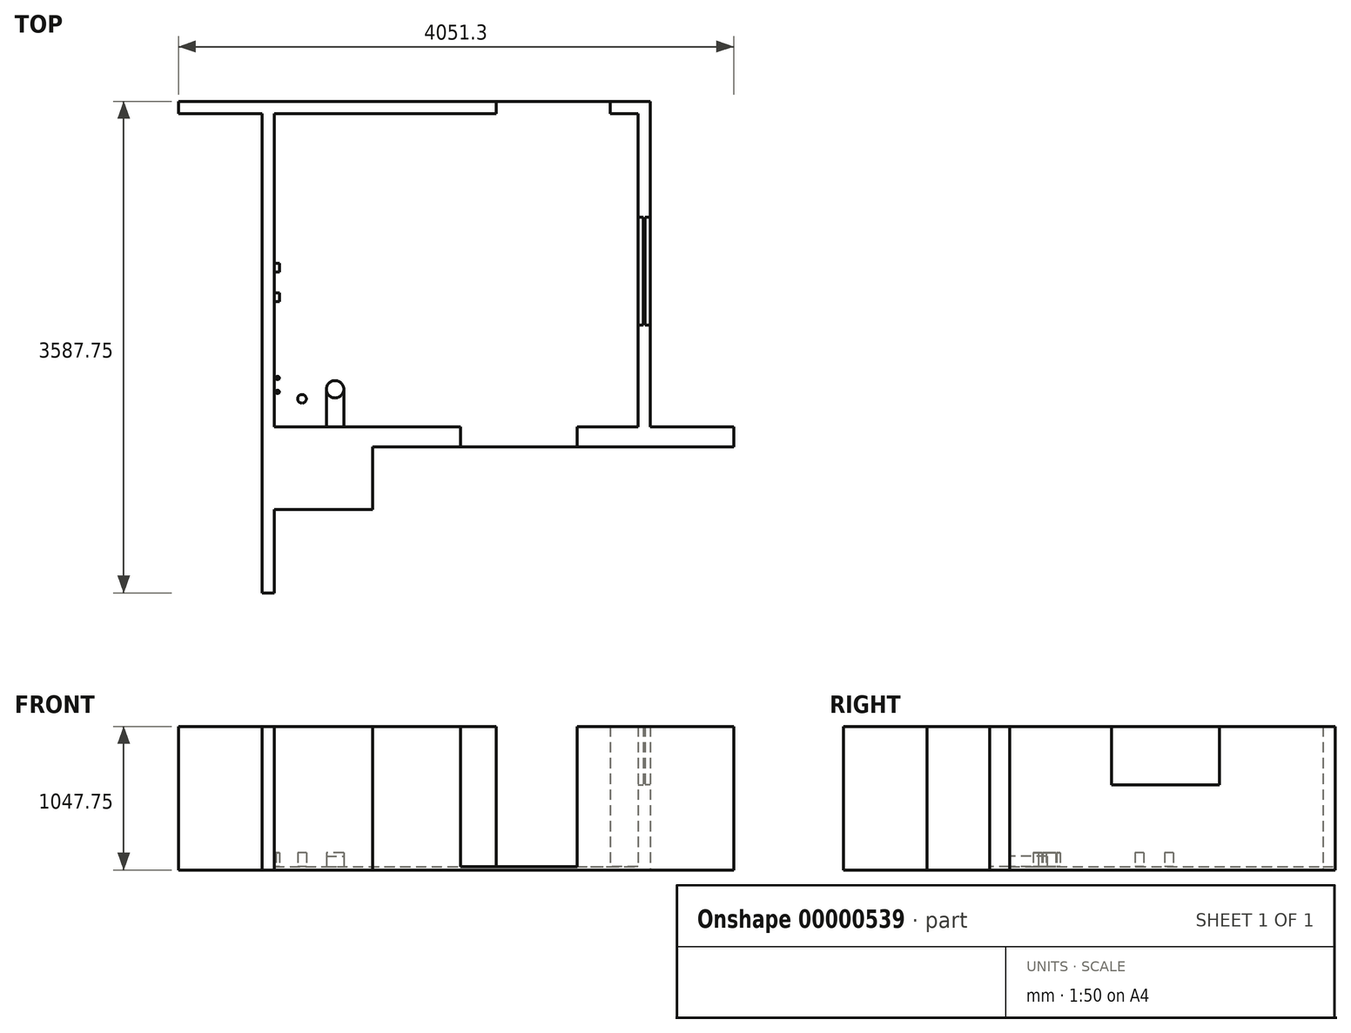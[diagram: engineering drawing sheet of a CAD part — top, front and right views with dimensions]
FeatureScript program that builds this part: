
annotation { "Feature Type Name" : "Feature", "Feature Type Description" : "" }
export const myFeature = defineFeature(function(context is Context, id is Id, definition is map)
    precondition{}
    {
        {
            var Q0;
            Q0=qCreatedBy(makeId("Top.planeOp"),FACE);
            var sketch = newSketch(context, id + "F0", { "sketchPlane" : qUnion([Q0])});
            skLineSegment(sketch, "E0.bottom", {"start": v(0, 2286) * mm, "end": v(1619.25, 2286) * mm});
            skLineSegment(sketch, "E0.top", {"start": v(0, 0) * mm, "end": v(1358.9, 0) * mm});
            skLineSegment(sketch, "E0.left", {"start": v(0, 2286) * mm, "end": v(0, 0) * mm});
            skLineSegment(sketch, "E1", {"start": v(1358.9, 0) * mm, "end": v(1358.9, -146.05) * mm});
            skLineSegment(sketch, "E2", {"start": v(1358.9, -146.05) * mm, "end": v(717.55, -146.05) * mm});
            skLineSegment(sketch, "E3", {"start": v(717.55, -146.05) * mm, "end": v(717.55, -603.25) * mm});
            skLineSegment(sketch, "E4", {"start": v(717.55, -603.25) * mm, "end": v(0, -603.25) * mm});
            skLineSegment(sketch, "E5", {"start": v(0, -603.25) * mm, "end": v(0, -1212.85) * mm});
            skLineSegment(sketch, "E6", {"start": v(2209.8, -146.05) * mm, "end": v(2209.8, 0) * mm});
            skLineSegment(sketch, "E7", {"start": v(2209.8, 0) * mm, "end": v(2654.3, 0) * mm});
            skLineSegment(sketch, "E8", {"start": v(2654.3, 0) * mm, "end": v(2654.3, 2286) * mm});
            skLineSegment(sketch, "E9", {"start": v(2654.3, 2286) * mm, "end": v(2451.1, 2286) * mm});
            skLineSegment(sketch, "E10", {"start": v(2451.1, 2286) * mm, "end": v(2451.1, 2374.9) * mm});
            skLineSegment(sketch, "E11", {"start": v(2451.1, 2374.9) * mm, "end": v(2743.2, 2374.9) * mm});
            skLineSegment(sketch, "E12", {"start": v(2743.2, 2374.9) * mm, "end": v(2743.2, 0) * mm});
            skLineSegment(sketch, "E13", {"start": v(2743.2, 0) * mm, "end": v(3352.8, 0) * mm});
            skLineSegment(sketch, "E14", {"start": v(1619.25, 2286) * mm, "end": v(1619.25, 2374.9) * mm});
            skLineSegment(sketch, "E15", {"start": v(1619.25, 2374.9) * mm, "end": v(-698.5, 2374.9) * mm});
            skLineSegment(sketch, "E16", {"start": v(-698.5, 2374.9) * mm, "end": v(-698.5, 2286) * mm});
            skLineSegment(sketch, "E17", {"start": v(-698.5, 2286) * mm, "end": v(-88.9, 2286) * mm});
            skLineSegment(sketch, "E18", {"start": v(-88.9, 2286) * mm, "end": v(-88.9, -1212.85) * mm});
            skLineSegment(sketch, "E19", {"start": v(2209.8, -146.05) * mm, "end": v(3352.8, -146.05) * mm});
            skLineSegment(sketch, "E20", {"start": v(3352.8, -146.05) * mm, "end": v(3352.8, 0) * mm});
            skLineSegment(sketch, "E21", {"start": v(-88.9, -1212.85) * mm, "end": v(0, -1212.85) * mm});
            skSolve(sketch);
        }
        {
            var Q0;
            Q0 = qSketchRegion(id + "F0", true);
            extrude(context, id + "F1", {"entities" : qUnion([Q0]), "depth" : 2241.55 * mm, "offsetDistance" : 25.4 * mm});
        }
        {
            var Q0;
            Q0=qCreatedBy(makeId("Top.planeOp"),FACE);
            var sketch = newSketch(context, id + "F2", { "sketchPlane" : qUnion([Q0])});
            skLineSegment(sketch, "E22.0", {"start": v(2743.2, 0) * mm, "end": v(3352.8, 0) * mm});
            skLineSegment(sketch, "E22.1", {"start": v(2743.2, 2374.9) * mm, "end": v(2743.2, 0) * mm});
            skLineSegment(sketch, "E22.2", {"start": v(2451.1, 2374.9) * mm, "end": v(2743.2, 2374.9) * mm});
            skLineSegment(sketch, "E22.3", {"start": v(-698.5, 2374.9) * mm, "end": v(-698.5, 2286) * mm});
            skLineSegment(sketch, "E22.4", {"start": v(-698.5, 2286) * mm, "end": v(-88.9, 2286) * mm});
            skLineSegment(sketch, "E22.5", {"start": v(-88.9, 2286) * mm, "end": v(-88.9, -1212.85) * mm});
            skLineSegment(sketch, "E23", {"start": v(-698.5, 2374.9) * mm, "end": v(2451.1, 2374.9) * mm});
            skLineSegment(sketch, "E24", {"start": v(3352.8, 0) * mm, "end": v(3352.8, -146.05) * mm});
            skLineSegment(sketch, "E25", {"start": v(3352.8, -146.05) * mm, "end": v(717.55, -146.05) * mm});
            skLineSegment(sketch, "E26", {"start": v(717.55, -146.05) * mm, "end": v(717.55, -603.25) * mm});
            skLineSegment(sketch, "E27", {"start": v(717.55, -603.25) * mm, "end": v(0, -603.25) * mm});
            skLineSegment(sketch, "E28", {"start": v(0, -603.25) * mm, "end": v(0, -1212.85) * mm});
            skLineSegment(sketch, "E29", {"start": v(0, -1212.85) * mm, "end": v(-88.9, -1212.85) * mm});
            skSolve(sketch);
        }
        {
            var Q0;
            Q0 = qSketchRegion(id + "F2", true);
            extrude(context, id + "F3", {"entities" : qUnion([Q0]), "oppositeDirection" : true, "depth" : 25.4 * mm, "offsetDistance" : 25.4 * mm});
        }
        {
            var Q0;
            Q0=makeQuery(id+"F1.opExtrude","SWEPT_BODY",BODY,{"disambiguationData":[OSD([sQuery(id+"F0.wireOp",EDGE,"E0.bottom"),sQuery(id+"F0.wireOp",EDGE,"E0.top"),sQuery(id+"F0.wireOp",EDGE,"E0.left"),sQuery(id+"F0.wireOp",EDGE,"E1"),sQuery(id+"F0.wireOp",EDGE,"E2"),sQuery(id+"F0.wireOp",EDGE,"E3"),sQuery(id+"F0.wireOp",EDGE,"E4"),sQuery(id+"F0.wireOp",EDGE,"E5"),sQuery(id+"F0.wireOp",EDGE,"E14"),sQuery(id+"F0.wireOp",EDGE,"E15"),sQuery(id+"F0.wireOp",EDGE,"E16"),sQuery(id+"F0.wireOp",EDGE,"E17"),sQuery(id+"F0.wireOp",EDGE,"E18"),sQuery(id+"F0.wireOp",EDGE,"E21")])]});
            var Q1;
            Q1=makeQuery(id+"F1.opExtrude","SWEPT_BODY",BODY,{"disambiguationData":[OSD([sQuery(id+"F0.wireOp",EDGE,"E6"),sQuery(id+"F0.wireOp",EDGE,"E7"),sQuery(id+"F0.wireOp",EDGE,"E8"),sQuery(id+"F0.wireOp",EDGE,"E9"),sQuery(id+"F0.wireOp",EDGE,"E10"),sQuery(id+"F0.wireOp",EDGE,"E11"),sQuery(id+"F0.wireOp",EDGE,"E12"),sQuery(id+"F0.wireOp",EDGE,"E13"),sQuery(id+"F0.wireOp",EDGE,"E19"),sQuery(id+"F0.wireOp",EDGE,"E20")])]});
            var Q2;
            Q2=makeQuery(id+"F3.opExtrude","SWEPT_BODY",BODY,{"disambiguationData":[OSD([sQuery(id+"F2.wireOp",EDGE,"E22.0"),sQuery(id+"F2.wireOp",EDGE,"E22.1"),sQuery(id+"F2.wireOp",EDGE,"E22.2"),sQuery(id+"F2.wireOp",EDGE,"E22.3"),sQuery(id+"F2.wireOp",EDGE,"E22.4"),sQuery(id+"F2.wireOp",EDGE,"E22.5"),sQuery(id+"F2.wireOp",EDGE,"E23"),sQuery(id+"F2.wireOp",EDGE,"E24"),sQuery(id+"F2.wireOp",EDGE,"E25"),sQuery(id+"F2.wireOp",EDGE,"E26"),sQuery(id+"F2.wireOp",EDGE,"E27"),sQuery(id+"F2.wireOp",EDGE,"E28"),sQuery(id+"F2.wireOp",EDGE,"E29")])]});
            booleanBodies(context, id + "F4", {"operationType" : BooleanOperationType.UNION, "tools" : qUnion([Q0, Q1, Q2])});
        }
        {
            var Q0;
            Q0=qCreatedBy(makeId("Top.planeOp"),FACE);
            cPlane(context, id + "F5", {"entities" : qUnion([Q0]), "cplaneType" : CPlaneType.OFFSET, "offset" : 596.9 * mm, "width" : 152.4 * mm, "height" : 152.4 * mm});
        }
        {
            var Q0;
            Q0=qCreatedBy(id+"F5.planeOp",FACE);
            var sketch = newSketch(context, id + "F6", { "sketchPlane" : qUnion([Q0])});
            skLineSegment(sketch, "E30.bottom", {"start": v(2654.3, 1530.35) * mm, "end": v(2692.4, 1530.35) * mm});
            skLineSegment(sketch, "E30.top", {"start": v(2654.3, 742.95) * mm, "end": v(2692.4, 742.95) * mm});
            skLineSegment(sketch, "E30.left", {"start": v(2654.3, 1530.35) * mm, "end": v(2654.3, 742.95) * mm});
            skLineSegment(sketch, "E30.right", {"start": v(2692.4, 1530.35) * mm, "end": v(2692.4, 742.95) * mm});
            skLineSegment(sketch, "E31.bottom", {"start": v(2743.2, 742.95) * mm, "end": v(2705.1, 742.95) * mm});
            skLineSegment(sketch, "E31.top", {"start": v(2743.2, 1530.35) * mm, "end": v(2705.1, 1530.35) * mm});
            skLineSegment(sketch, "E31.left", {"start": v(2743.2, 742.95) * mm, "end": v(2743.2, 1530.35) * mm});
            skLineSegment(sketch, "E31.right", {"start": v(2705.1, 742.95) * mm, "end": v(2705.1, 1530.35) * mm});
            skSolve(sketch);
        }
        {
            var Q0;
            Q0 = qSketchRegion(id + "F6", true);
            extrude(context, id + "F7", {"entities" : qUnion([Q0]), "operationType" : NewBodyOperationType.REMOVE, "depth" : 1244.6 * mm, "offsetDistance" : 25.4 * mm});
        }
        {
            var Q0;
            Q0=makeQuery(id+"F3.opExtrude","CAP_FACE",FACE,{"disambiguationData":[OSD([sQuery(id+"F2.wireOp",EDGE,"E22.0"),sQuery(id+"F2.wireOp",EDGE,"E22.1"),sQuery(id+"F2.wireOp",EDGE,"E22.2"),sQuery(id+"F2.wireOp",EDGE,"E22.3"),sQuery(id+"F2.wireOp",EDGE,"E22.4"),sQuery(id+"F2.wireOp",EDGE,"E22.5"),sQuery(id+"F2.wireOp",EDGE,"E23"),sQuery(id+"F2.wireOp",EDGE,"E24"),sQuery(id+"F2.wireOp",EDGE,"E25"),sQuery(id+"F2.wireOp",EDGE,"E26"),sQuery(id+"F2.wireOp",EDGE,"E27"),sQuery(id+"F2.wireOp",EDGE,"E28"),sQuery(id+"F2.wireOp",EDGE,"E29")])],"isStart":true});
            var sketch = newSketch(context, id + "F8", { "sketchPlane" : qUnion([Q0])});
            skPoint(sketch, "E32.oppositeSnap0", {"position": v(0, 1130.3) * mm});
            skLineSegment(sketch, "E32.bottom", {"start": v(0, 1193.8) * mm, "end": v(38.1, 1193.8) * mm});
            skLineSegment(sketch, "E32.top", {"start": v(0, 1130.3) * mm, "end": v(38.1, 1130.3) * mm});
            skLineSegment(sketch, "E32.left", {"start": v(0, 1193.8) * mm, "end": v(0, 1130.3) * mm});
            skLineSegment(sketch, "E32.right", {"start": v(38.1, 1193.8) * mm, "end": v(38.1, 1130.3) * mm});
            skLineSegment(sketch, "E33.bottom", {"start": v(0, 914.4) * mm, "end": v(38.1, 914.4) * mm});
            skLineSegment(sketch, "E33.top", {"start": v(0, 977.9) * mm, "end": v(38.1, 977.9) * mm});
            skLineSegment(sketch, "E33.left", {"start": v(0, 914.4) * mm, "end": v(0, 977.9) * mm});
            skLineSegment(sketch, "E33.right", {"start": v(38.1, 914.4) * mm, "end": v(38.1, 977.9) * mm});
            skCircle(sketch, "E34", {"center": v(25.4, 254) * mm, "radius": 12.7 * mm});
            skCircle(sketch, "E35", {"center": v(203.2, 203.2) * mm, "radius": 31.75 * mm});
            skCircle(sketch, "E36", {"center": v(444.5, 273.05) * mm, "radius": 63.5 * mm});
            skCircle(sketch, "E37", {"center": v(25.4, 355.6) * mm, "radius": 12.7 * mm});
            skLineSegment(sketch, "E38.bottom", {"start": v(381, 273.05) * mm, "end": v(508, 273.05) * mm});
            skLineSegment(sketch, "E38.top", {"start": v(381, 0) * mm, "end": v(508, 0) * mm});
            skLineSegment(sketch, "E38.left", {"start": v(381, 273.05) * mm, "end": v(381, 0) * mm});
            skLineSegment(sketch, "E38.right", {"start": v(508, 273.05) * mm, "end": v(508, 0) * mm});
            skSolve(sketch);
        }
        {
            var Q0;
            Q0=makeQuery(id+"F8.imprint","IMPRINT",FACE,{"disambiguationData":[TD([[makeQuery(id+"F8.imprint","IMPRINT",EDGE,{"derivedFrom":sQuery(id+"F8.wireOp",EDGE,"E32.bottom")}),-1.0]])]});
            var Q1;
            Q1=makeQuery(id+"F8.imprint","IMPRINT",FACE,{"disambiguationData":[TD([[makeQuery(id+"F8.imprint","IMPRINT",EDGE,{"derivedFrom":sQuery(id+"F8.wireOp",EDGE,"E33.bottom")}),1.0]])]});
            var Q2;
            Q2=makeQuery(id+"F8.imprint","IMPRINT",FACE,{"disambiguationData":[TD([[makeQuery(id+"F8.imprint","IMPRINT",EDGE,{"derivedFrom":sQuery(id+"F8.wireOp",EDGE,"E34")}),1.0]])]});
            var Q3;
            Q3=makeQuery(id+"F8.imprint","IMPRINT",FACE,{"disambiguationData":[TD([[makeQuery(id+"F8.imprint","IMPRINT",EDGE,{"derivedFrom":sQuery(id+"F8.wireOp",EDGE,"E35")}),1.0]])]});
            var Q4;
            Q4=makeQuery(id+"F8.imprint","IMPRINT",FACE,{"disambiguationData":[TD([[makeQuery(id+"F8.imprint","IMPRINT",EDGE,{"derivedFrom":sQuery(id+"F8.wireOp",EDGE,"E37")}),1.0]])]});
            var Q5;
            {var subQ0=sQuery(id+"F8.wireOp",EDGE,"E38.bottom");Q5=makeQuery(id+"F8.imprint","IMPRINT",FACE,{"disambiguationData":[TD([[makeQuery(id+"F8.imprint","IMPRINT",EDGE,{"derivedFrom":subQ0}),1.0]])]});}
            var Q6;
            {var subQ0=sQuery(id+"F8.wireOp",EDGE,"E38.bottom");Q6=makeQuery(id+"F8.imprint","IMPRINT",FACE,{"disambiguationData":[TD([[makeQuery(id+"F8.imprint","IMPRINT",EDGE,{"derivedFrom":subQ0}),-1.0]])]});}
            extrude(context, id + "F9", {"entities" : qUnion([Q0, Q1, Q2, Q3, Q4, Q5, Q6]), "depth" : 101.6 * mm, "offsetDistance" : 25.4 * mm});
        }
        {
            var Q0;
            Q0=makeQuery(id+"F8.imprint","IMPRINT",FACE,{"disambiguationData":[TD([[makeQuery(id+"F8.imprint","IMPRINT",EDGE,{"derivedFrom":sQuery(id+"F8.wireOp",EDGE,"E38.top")}),1.0]])]});
            extrude(context, id + "F10", {"entities" : qUnion([Q0]), "depth" : 76.2 * mm, "offsetDistance" : 25.4 * mm});
        }
        {
            var Q0;
            Q0=makeQuery(id+"F1.opExtrude","CAP_FACE",FACE,{"disambiguationData":[OSD([sQuery(id+"F0.wireOp",EDGE,"E0.bottom"),sQuery(id+"F0.wireOp",EDGE,"E0.top"),sQuery(id+"F0.wireOp",EDGE,"E0.left"),sQuery(id+"F0.wireOp",EDGE,"E1"),sQuery(id+"F0.wireOp",EDGE,"E2"),sQuery(id+"F0.wireOp",EDGE,"E3"),sQuery(id+"F0.wireOp",EDGE,"E4"),sQuery(id+"F0.wireOp",EDGE,"E5"),sQuery(id+"F0.wireOp",EDGE,"E14"),sQuery(id+"F0.wireOp",EDGE,"E15"),sQuery(id+"F0.wireOp",EDGE,"E16"),sQuery(id+"F0.wireOp",EDGE,"E17"),sQuery(id+"F0.wireOp",EDGE,"E18"),sQuery(id+"F0.wireOp",EDGE,"E21")])],"isStart":false});
            var sketch = newSketch(context, id + "F11", { "sketchPlane" : qUnion([Q0])});
            skLineSegment(sketch, "E39.bottom", {"start": v(-698.5, 2374.9) * mm, "end": v(3352.8, 2374.9) * mm});
            skLineSegment(sketch, "E39.top", {"start": v(-698.5, -1212.85) * mm, "end": v(3352.8, -1212.85) * mm});
            skLineSegment(sketch, "E39.left", {"start": v(-698.5, 2374.9) * mm, "end": v(-698.5, -1212.85) * mm});
            skLineSegment(sketch, "E39.right", {"start": v(3352.8, 2374.9) * mm, "end": v(3352.8, -1212.85) * mm});
            skSolve(sketch);
        }
        {
            var Q0;
            Q0 = qSketchRegion(id + "F11", true);
            extrude(context, id + "F12", {"entities" : qUnion([Q0]), "operationType" : NewBodyOperationType.REMOVE, "oppositeDirection" : true, "depth" : 1219.2 * mm, "offsetDistance" : 25.4 * mm});
        }
    });
